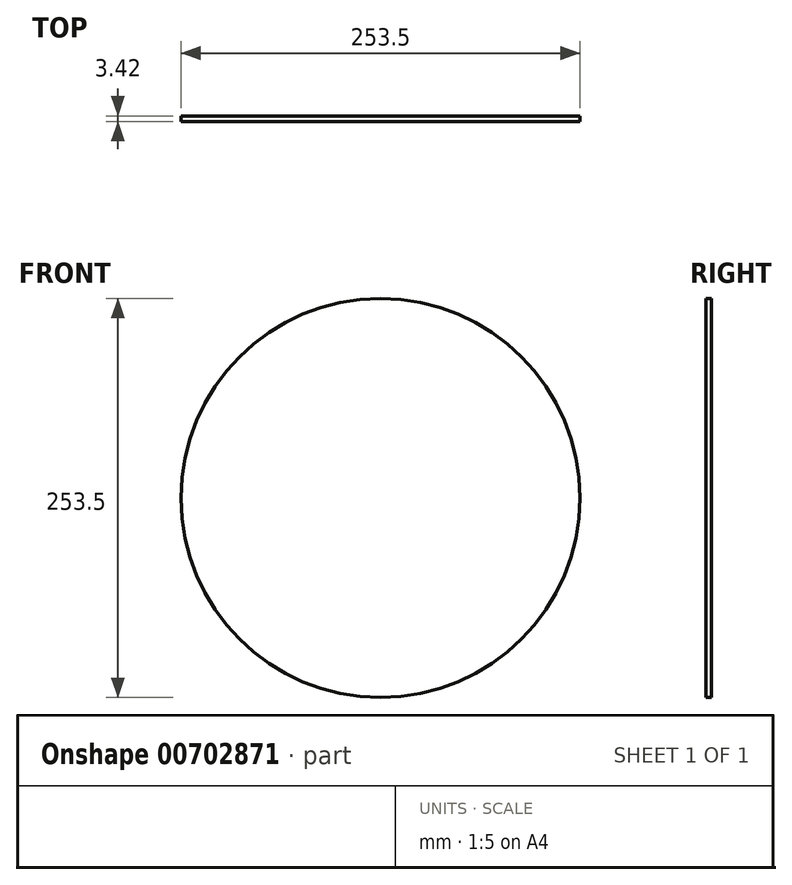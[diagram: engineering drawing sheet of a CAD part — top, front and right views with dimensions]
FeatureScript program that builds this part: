
annotation { "Feature Type Name" : "Feature", "Feature Type Description" : "" }
export const myFeature = defineFeature(function(context is Context, id is Id, definition is map)
    precondition{}
    {
        {
            var Q0;
            Q0=qCreatedBy(makeId("Front.planeOp"),FACE);
            var sketch = newSketch(context, id + "F0", { "sketchPlane" : qUnion([Q0])});
            skCircle(sketch, "E0", {"center": v(0, 0) * mm, "radius": 126.75 * mm});
            skSolve(sketch);
        }
        {
            var Q0;
            Q0 = qSketchRegion(id + "F0", true);
            extrude(context, id + "F1", {"entities" : qUnion([Q0]), "depth" : 3.42 * mm, "offsetDistance" : 25.4 * mm});
        }
    });
